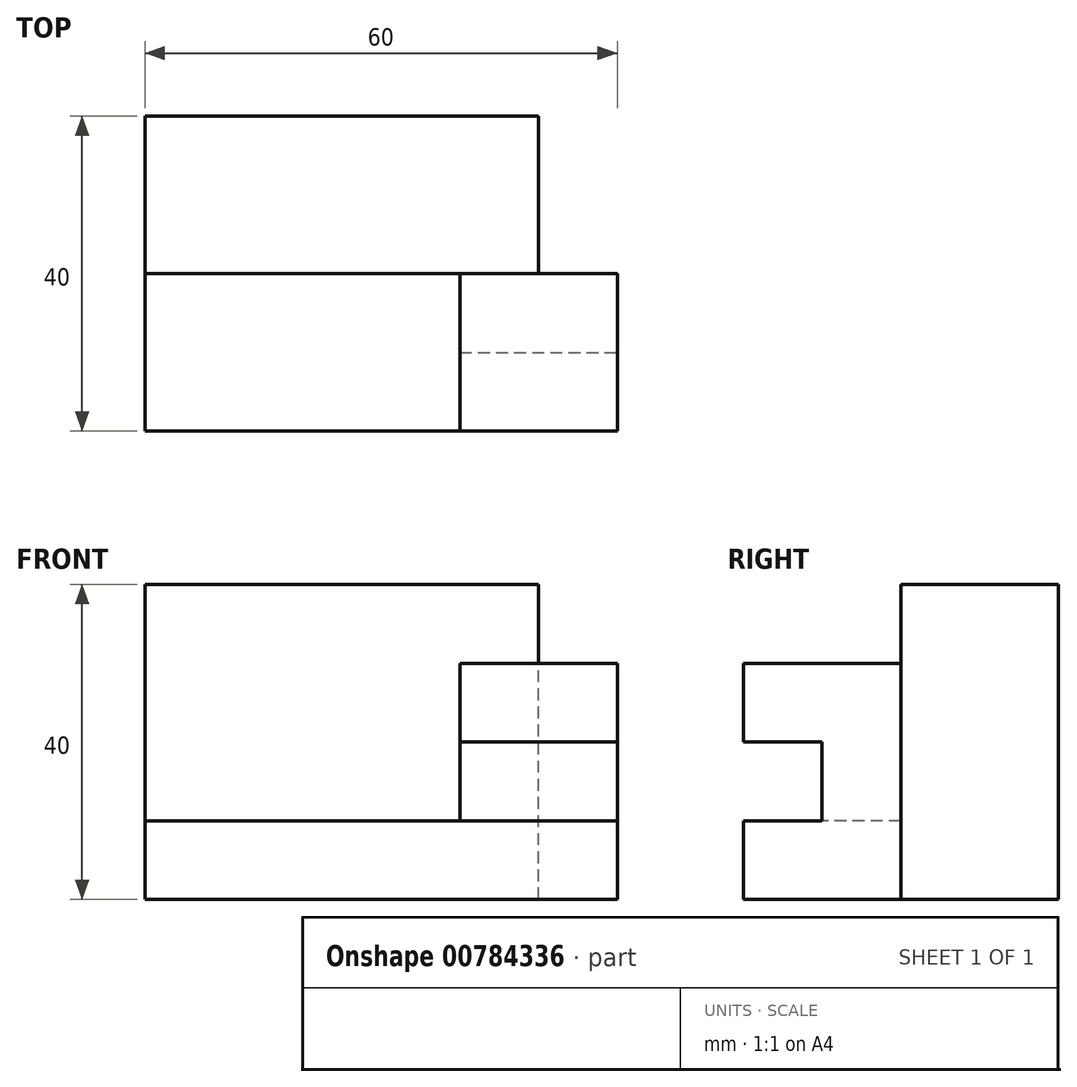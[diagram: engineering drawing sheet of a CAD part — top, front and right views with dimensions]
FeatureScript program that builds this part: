
annotation { "Feature Type Name" : "Feature", "Feature Type Description" : "" }
export const myFeature = defineFeature(function(context is Context, id is Id, definition is map)
    precondition{}
    {
        {
            var Q0;
            Q0=qCreatedBy(makeId("Top.planeOp"),FACE);
            var sketch = newSketch(context, id + "F0", { "sketchPlane" : qUnion([Q0])});
            skLineSegment(sketch, "E0", {"start": v(0, 0) * mm, "end": v(0, 40) * mm});
            skLineSegment(sketch, "E1", {"start": v(0, 40) * mm, "end": v(60, 40) * mm});
            skLineSegment(sketch, "E2", {"start": v(60, 40) * mm, "end": v(60, 0) * mm});
            skLineSegment(sketch, "E3", {"start": v(60, 0) * mm, "end": v(0, 0) * mm});
            skSolve(sketch);
        }
        {
            var Q0;
            Q0=makeQuery(id+"F0.imprint","IMPRINT",FACE,{"disambiguationData":[TD([[makeQuery(id+"F0.imprint","IMPRINT",EDGE,{"derivedFrom":sQuery(id+"F0.wireOp",EDGE,"E0")}),-1.0]])]});
            extrude(context, id + "F1", {"entities" : qUnion([Q0]), "depth" : 40 * mm, "offsetDistance" : 25 * mm});
        }
        {
            var Q0;
            Q0=makeQuery(id+"F1.opExtrude","CAP_FACE",FACE,{"disambiguationData":[OSD([sQuery(id+"F0.wireOp",EDGE,"E0"),sQuery(id+"F0.wireOp",EDGE,"E1"),sQuery(id+"F0.wireOp",EDGE,"E2"),sQuery(id+"F0.wireOp",EDGE,"E3")])],"isStart":false});
            var sketch = newSketch(context, id + "F2", { "sketchPlane" : qUnion([Q0])});
            skLineSegment(sketch, "E4", {"start": v(60, 40) * mm, "end": v(60, 20) * mm});
            skLineSegment(sketch, "E5", {"start": v(60, 20) * mm, "end": v(50, 20) * mm});
            skLineSegment(sketch, "E6", {"start": v(50, 20) * mm, "end": v(50, 40) * mm});
            skLineSegment(sketch, "E7", {"start": v(50, 40) * mm, "end": v(60, 40) * mm});
            skSolve(sketch);
        }
        {
            var Q0;
            Q0=makeQuery(id+"F2.imprint","IMPRINT",FACE,{"disambiguationData":[TD([[makeQuery(id+"F2.imprint","IMPRINT",EDGE,{"derivedFrom":sQuery(id+"F2.wireOp",EDGE,"E4")}),-1.0]])]});
            extrude(context, id + "F3", {"entities" : qUnion([Q0]), "operationType" : NewBodyOperationType.REMOVE, "oppositeDirection" : true, "depth" : 45 * mm, "offsetDistance" : 25 * mm});
        }
        {
            var Q0;
            Q0=makeQuery(id+"F1.opExtrude","CAP_FACE",FACE,{"disambiguationData":[OSD([sQuery(id+"F0.wireOp",EDGE,"E0"),sQuery(id+"F0.wireOp",EDGE,"E1"),sQuery(id+"F0.wireOp",EDGE,"E2"),sQuery(id+"F0.wireOp",EDGE,"E3")])],"isStart":false});
            var sketch = newSketch(context, id + "F4", { "sketchPlane" : qUnion([Q0])});
            skLineSegment(sketch, "E8", {"start": v(0, 0) * mm, "end": v(0, 20) * mm});
            skLineSegment(sketch, "E9", {"start": v(0, 20) * mm, "end": v(40, 20) * mm});
            skLineSegment(sketch, "E10", {"start": v(40, 20) * mm, "end": v(40, 0) * mm});
            skLineSegment(sketch, "E11", {"start": v(40, 0) * mm, "end": v(0, 0) * mm});
            skSolve(sketch);
        }
        {
            var Q0;
            Q0=makeQuery(id+"F4.imprint","IMPRINT",FACE,{"disambiguationData":[TD([[makeQuery(id+"F4.imprint","IMPRINT",EDGE,{"derivedFrom":sQuery(id+"F4.wireOp",EDGE,"E8")}),-1.0]])]});
            extrude(context, id + "F5", {"entities" : qUnion([Q0]), "operationType" : NewBodyOperationType.REMOVE, "oppositeDirection" : true, "depth" : 30 * mm, "offsetDistance" : 25 * mm});
        }
        {
            var Q0;
            Q0=makeQuery(id+"F1.opExtrude","CAP_FACE",FACE,{"disambiguationData":[OSD([sQuery(id+"F0.wireOp",EDGE,"E0"),sQuery(id+"F0.wireOp",EDGE,"E1"),sQuery(id+"F0.wireOp",EDGE,"E2"),sQuery(id+"F0.wireOp",EDGE,"E3")])],"isStart":false});
            var sketch = newSketch(context, id + "F6", { "sketchPlane" : qUnion([Q0])});
            skLineSegment(sketch, "E12", {"start": v(40, 20) * mm, "end": v(60, 20) * mm});
            skLineSegment(sketch, "E13", {"start": v(60, 20) * mm, "end": v(60, 0) * mm});
            skLineSegment(sketch, "E14", {"start": v(60, 0) * mm, "end": v(40, 0) * mm});
            skLineSegment(sketch, "E15", {"start": v(40, 0) * mm, "end": v(40, 20) * mm});
            skSolve(sketch);
        }
        {
            var Q0;
            {var subQ0=sQuery(id+"F6.wireOp",EDGE,"E13");Q0=makeQuery(id+"F6.imprint","IMPRINT",FACE,{"disambiguationData":[TD([[makeQuery(id+"F6.imprint","IMPRINT",EDGE,{"derivedFrom":subQ0}),-1.0]])]});}
            extrude(context, id + "F7", {"entities" : qUnion([Q0]), "operationType" : NewBodyOperationType.REMOVE, "oppositeDirection" : true, "depth" : 10 * mm, "offsetDistance" : 25 * mm});
        }
        {
            var Q0;
            Q0=makeQuery(id+"F1.opExtrude","SWEPT_FACE",FACE,{"disambiguationData":[OSD([sQuery(id+"F0.wireOp",EDGE,"E2")])]});
            var sketch = newSketch(context, id + "F8", { "sketchPlane" : qUnion([Q0])});
            skLineSegment(sketch, "E16.bottom", {"start": v(0, 10) * mm, "end": v(10, 10) * mm});
            skLineSegment(sketch, "E16.top", {"start": v(0, 20) * mm, "end": v(10, 20) * mm});
            skLineSegment(sketch, "E16.left", {"start": v(0, 10) * mm, "end": v(0, 20) * mm});
            skLineSegment(sketch, "E16.right", {"start": v(10, 10) * mm, "end": v(10, 20) * mm});
            skSolve(sketch);
        }
        {
            var Q0;
            Q0=makeQuery(id+"F8.imprint","IMPRINT",FACE,{"disambiguationData":[TD([[makeQuery(id+"F8.imprint","IMPRINT",EDGE,{"derivedFrom":sQuery(id+"F8.wireOp",EDGE,"E16.bottom")}),1.0]])]});
            extrude(context, id + "F9", {"entities" : qUnion([Q0]), "operationType" : NewBodyOperationType.REMOVE, "oppositeDirection" : true, "depth" : 25 * mm, "offsetDistance" : 25 * mm});
        }
    });
